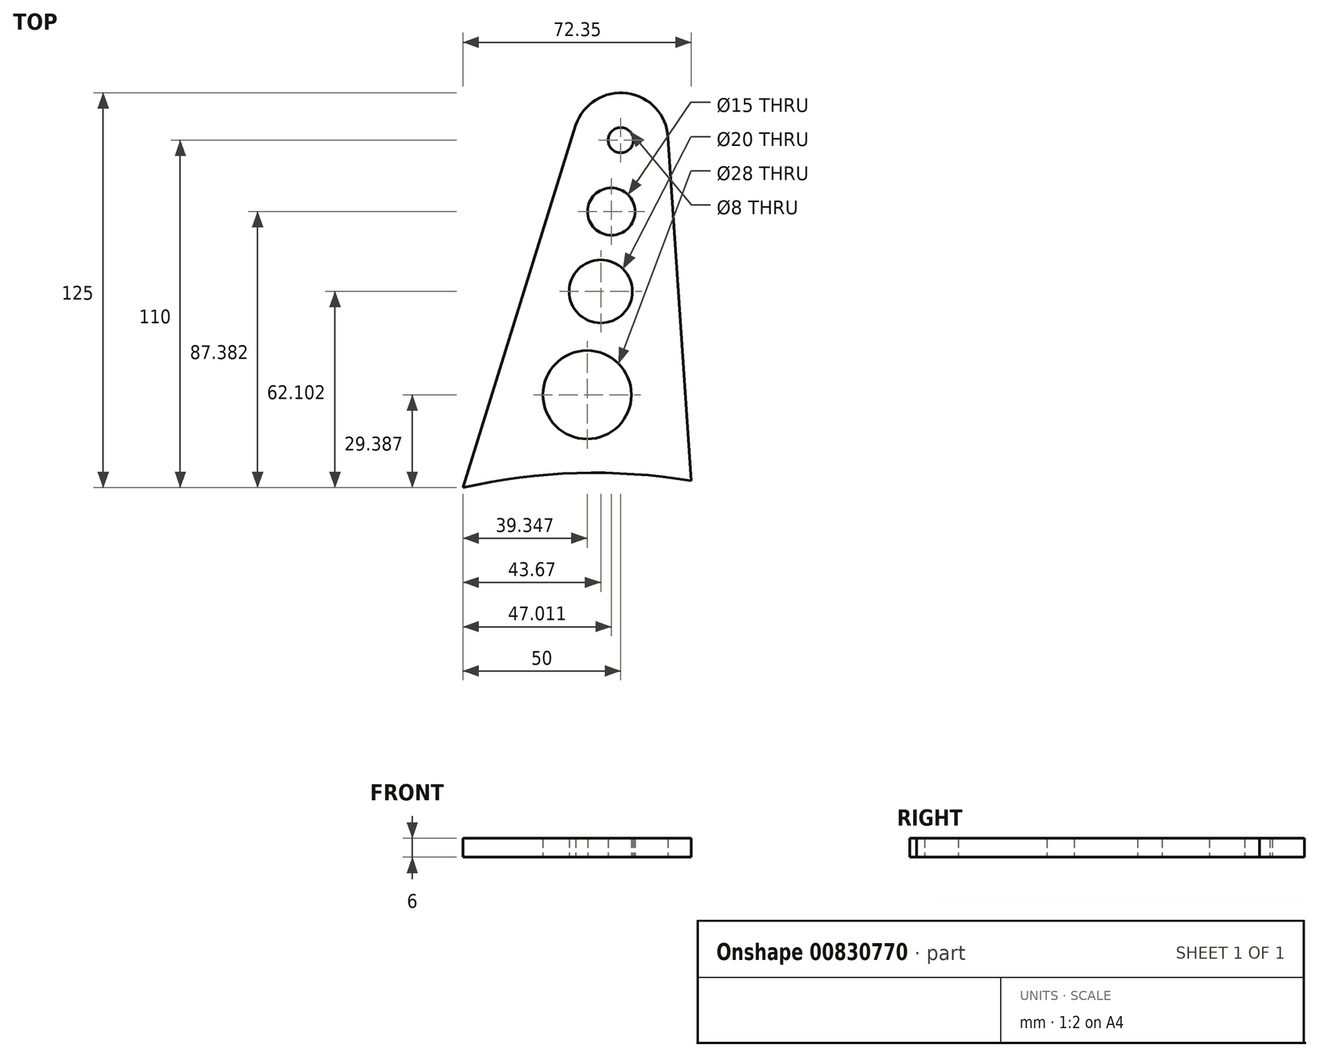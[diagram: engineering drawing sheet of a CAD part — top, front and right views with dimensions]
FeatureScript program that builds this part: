
annotation { "Feature Type Name" : "Feature", "Feature Type Description" : "" }
export const myFeature = defineFeature(function(context is Context, id is Id, definition is map)
    precondition{}
    {
        {
            var Q0;
            Q0=qCreatedBy(makeId("Top.planeOp"),FACE);
            var sketch = newSketch(context, id + "F0", { "sketchPlane" : qUnion([Q0])});
            skCircle(sketch, "E0", {"center": v(0, 0) * mm, "radius": 4 * mm});
            skArc(sketch, "E1", {"start": v(14.98, 0.76) * mm, "mid": v(2.04, 14.86) * mm, "end": v(-14.22, 4.76) * mm});
            skLineSegment(sketch, "E2", {"start": v(-50, -110) * mm, "end": v(-14.22, 4.76) * mm});
            skLineSegment(sketch, "E3", {"start": v(22.35, -107.85) * mm, "end": v(14.98, 0.76) * mm});
            skArc(sketch, "E4", {"start": v(22.35, -107.85) * mm, "mid": v(-13.93, -105.4) * mm, "end": v(-50, -110) * mm});
            skPoint(sketch, "E4.third.point", {"position": v(-13.93, -480.23) * mm});
            skLineSegment(sketch, "E5", {"start": v(0, 0) * mm, "end": v(-13.93, -105.4) * mm});
            skCircle(sketch, "E6", {"center": v(-2.99, -22.62) * mm, "radius": 7.5 * mm});
            skCircle(sketch, "E7", {"center": v(-6.33, -47.9) * mm, "radius": 10 * mm});
            skCircle(sketch, "E8", {"center": v(-10.65, -80.61) * mm, "radius": 14 * mm});
            skSolve(sketch);
        }
        {
            var Q0;
            Q0 = qSketchRegion(id + "F0", true);
            extrude(context, id + "F1", {"entities" : qUnion([Q0]), "depth" : 6 * mm, "offsetDistance" : 25 * mm});
        }
    });
